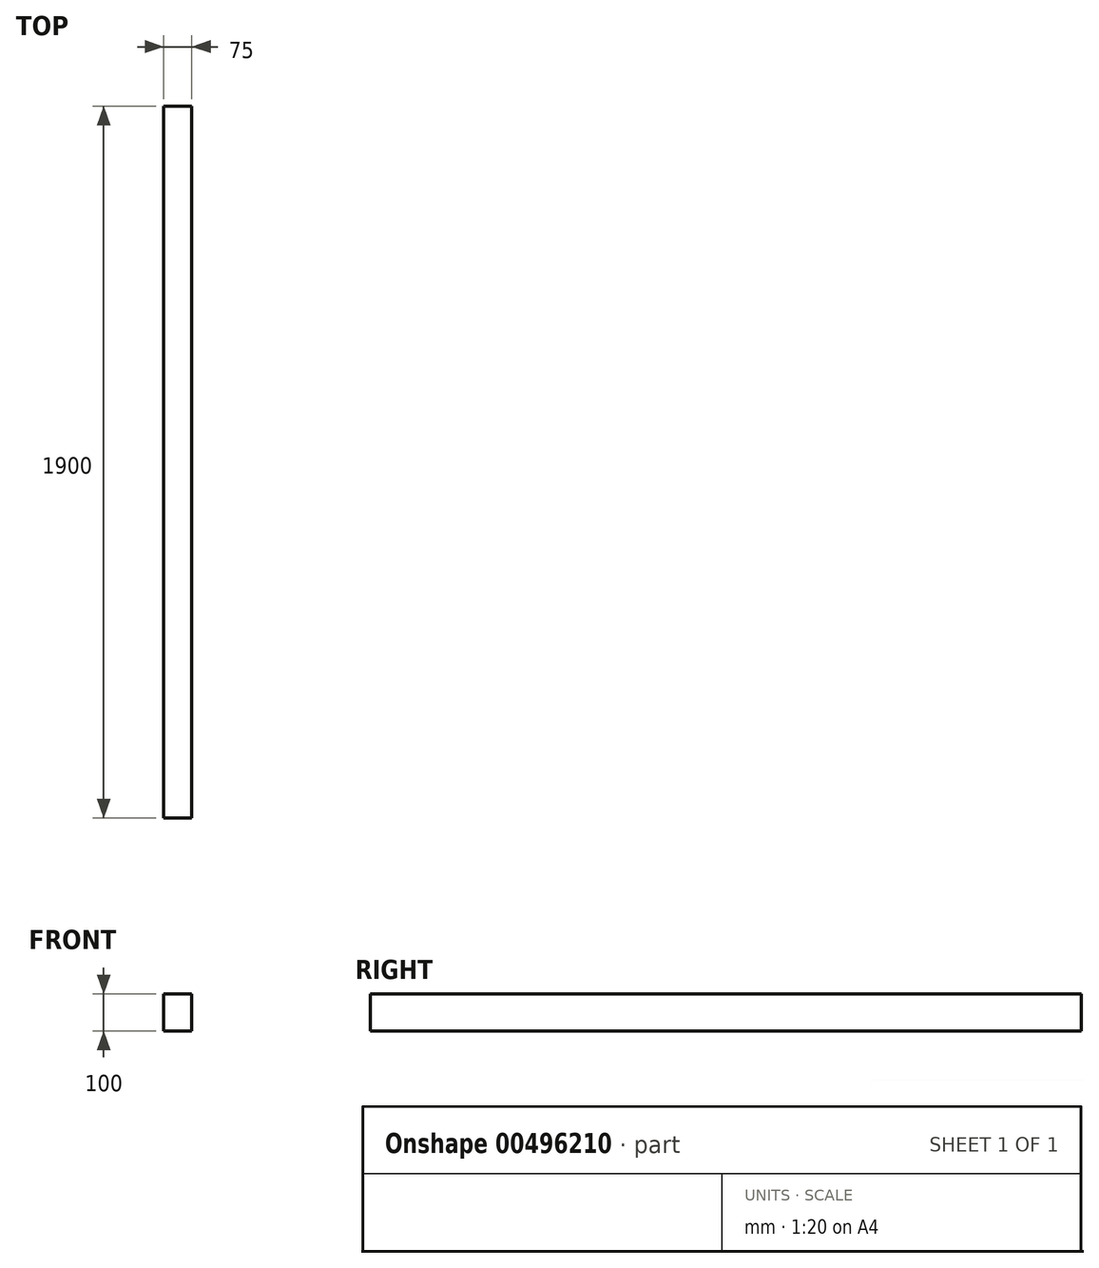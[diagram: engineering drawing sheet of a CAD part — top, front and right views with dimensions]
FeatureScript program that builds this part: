
annotation { "Feature Type Name" : "Feature", "Feature Type Description" : "" }
export const myFeature = defineFeature(function(context is Context, id is Id, definition is map)
    precondition{}
    {
        {
            var Q0;
            Q0=qCreatedBy(makeId("Front.planeOp"),FACE);
            var sketch = newSketch(context, id + "F0", { "sketchPlane" : qUnion([Q0])});
            skLineSegment(sketch, "E0.bottom", {"start": v(-37.5, 0) * mm, "end": v(37.5, 0) * mm});
            skLineSegment(sketch, "E0.top", {"start": v(-37.5, -100) * mm, "end": v(37.5, -100) * mm});
            skLineSegment(sketch, "E0.left", {"start": v(-37.5, 0) * mm, "end": v(-37.5, -100) * mm});
            skLineSegment(sketch, "E0.right", {"start": v(37.5, 0) * mm, "end": v(37.5, -100) * mm});
            skSolve(sketch);
        }
        {
            var Q0;
            Q0 = qSketchRegion(id + "F0", true);
            extrude(context, id + "F1", {"entities" : qUnion([Q0]), "depth" : 1900 * mm, "offsetDistance" : 25.4 * mm});
        }
    });
